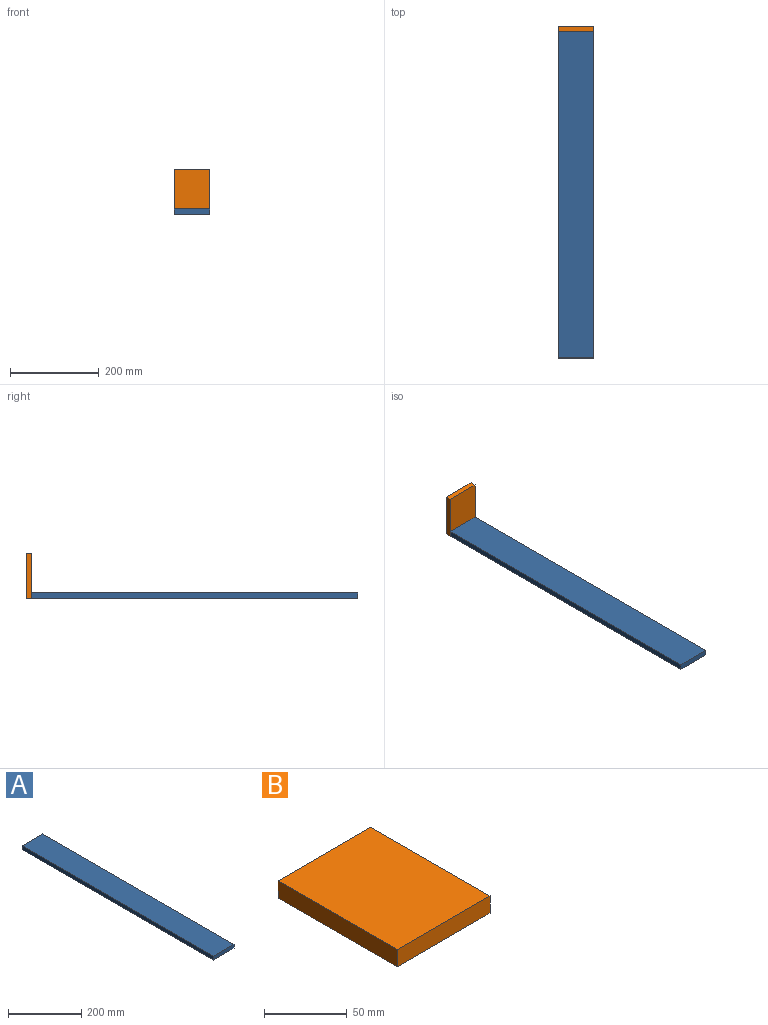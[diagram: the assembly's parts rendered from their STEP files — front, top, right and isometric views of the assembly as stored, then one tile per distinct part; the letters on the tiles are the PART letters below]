
ASSEMBLY  parts=2 mates=1
PART A: 6 faces, bbox 79.4x736.6x12.7 mm
  f0: plane 736.6x79.38mm, normal (0,0,1), area 58467.6mm2, adj f1,f3,f4,f5
  f1: plane 736.6x12.7mm, normal (-1,0,0), area 9354.8mm2, adj f0,f2,f4,f5
  f2: plane 736.6x79.38mm, normal (0,0,-1), area 58467.6mm2, adj f1,f3,f4,f5
  f3: plane 736.6x12.7mm, normal (1,0,0), area 9354.8mm2, adj f0,f2,f4,f5
  f4: plane 79.38x12.7mm, normal (0,-1,0), area 1008.1mm2, adj f0,f1,f2,f3
  f5: plane 79.38x12.7mm, normal (0,1,0), area 1008.1mm2, adj f0,f1,f2,f3
PART B: 6 faces, bbox 79.4x101.6x12.7 mm
  f0: plane 101.6x79.38mm, normal (0,0,1), area 8064.5mm2, adj f1,f3,f4,f5
  f1: plane 101.6x12.7mm, normal (-1,0,0), area 1290.3mm2, adj f0,f2,f4,f5
  f2: plane 101.6x79.38mm, normal (0,0,-1), area 8064.5mm2, adj f1,f3,f4,f5
  f3: plane 101.6x12.7mm, normal (1,0,0), area 1290.3mm2, adj f0,f2,f4,f5
  f4: plane 79.38x12.7mm, normal (0,-1,0), area 1008.1mm2, adj f0,f1,f2,f3
  f5: plane 79.38x12.7mm, normal (0,1,0), area 1008.1mm2, adj f0,f1,f2,f3
PLACE A t=(-237.09,157.3,-97.34)mm
PLACE B rot(axis=(1,0,0),90deg) t=(-215.65,155.32,-18.75)mm
MATE slider B.f0 <-> A.f5  axis (0,-1,0) through (-194.14,157.3,-120.35)mm
